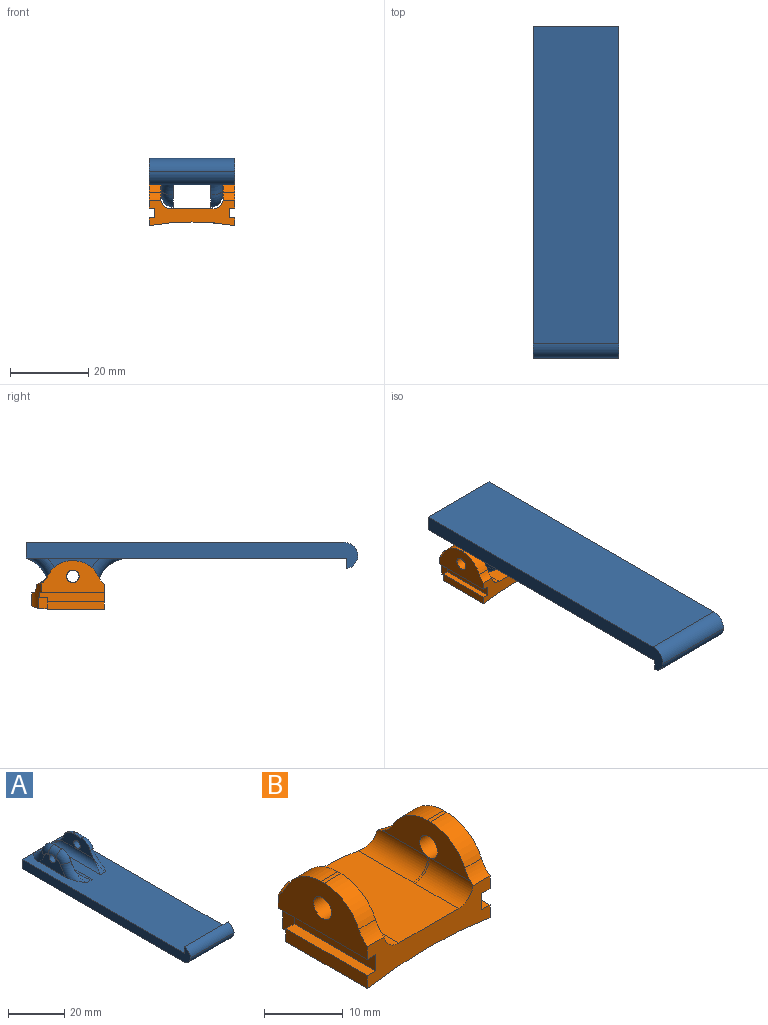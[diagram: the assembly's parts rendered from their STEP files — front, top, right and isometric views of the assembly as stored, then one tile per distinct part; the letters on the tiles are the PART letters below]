
ASSEMBLY  parts=2 mates=1
PART A: 36 faces, bbox 22x85x14.6 mm
  f0: plane 82x22mm, normal (0,0,1), area 1528.8mm2, adj f1,f2,f3,f5,f9,f17,f20,f22
  f1: plane 22x4mm, normal (0,1,0), area 88mm2, adj f0,f2,f3,f4,f21,f23
  f2: plane 84.99x6.8mm, normal (-1,0,0), area 342.9mm2, adj f0,f1,f4,f17,f18,f19
  f3: plane 84.99x6.8mm, normal (1,0,0), area 342.9mm2, adj f0,f1,f4,f17,f18,f19
  f4: plane 81.38x22mm, normal (0,0,-1), area 1790.3mm2, adj f1,f2,f3,f19
  f5: plane 13.57x5.6mm, normal (-1,0,0), area 46.2mm2, adj f0,f12,f31,f32,f33,f34,f35
  f6: plane 16.49x5.84mm, normal (1,0,0), area 65.3mm2, adj f7,f12,f13,f14,f20,f21,f24
  f7: plane 4x0.1mm, normal (0,0,1), area 0.4mm2, adj f6,f13,f14,f33
  f8: plane 16.49x5.84mm, normal (-1,0,0), area 65.3mm2, adj f10,f11,f15,f16,f22,f23,f25
  f9: plane 13.57x5.6mm, normal (1,0,0), area 46.2mm2, adj f0,f11,f26,f27,f28,f29,f30
  f10: plane 4x0.1mm, normal (0,0,1), area 0.4mm2, adj f8,f15,f16,f28
  f11: cylinder r=1.6mm len=3.2mm, axis (-1,0,0), area 30mm2, adj f8,f9,f28
  f12: cylinder r=1.6mm len=3.2mm, axis (-1,0,0), area 30mm2, adj f5,f6,f33
  f13: cylinder r=5mm len=4.65mm, axis (-1,0,0), area 0.6mm2, adj f6,f7,f20,f32
  f14: cylinder r=5mm len=4.71mm, axis (1,0,0), area 0.6mm2, adj f6,f7,f21,f34
  f15: cylinder r=5mm len=4.65mm, axis (-1,0,0), area 0.6mm2, adj f8,f10,f22,f27
  f16: cylinder r=5mm len=4.71mm, axis (1,0,0), area 0.6mm2, adj f8,f10,f23,f29
  f17: plane 22x2.8mm, normal (0,1,0), area 61.6mm2, adj f0,f2,f3,f18
  f18: cylinder r=3.62mm len=22mm, axis (-1,0,0), area 107.1mm2, adj f2,f3,f17,f19
  f19: cylinder r=3.62mm len=22mm, axis (1,0,0), area 120.9mm2, adj f2,f3,f4,f18
  f20: cylinder r=8.45mm len=7.86mm, axis (-1,0,0), area 8.1mm2, adj f0,f6,f13,f24,f31
  f21: cylinder r=8.45mm len=5.28mm, axis (-1,0,0), area 4.2mm2, adj f1,f6,f14,f24,f35
  f22: cylinder r=8.45mm len=7.86mm, axis (-1,0,0), area 8.1mm2, adj f0,f8,f15,f25,f26
  f23: cylinder r=8.45mm len=5.28mm, axis (-1,0,0), area 4.2mm2, adj f1,f8,f16,f25,f30
  f24: cylinder r=2.66mm len=26.49mm, axis (0,1,0), area 89.2mm2, adj f0,f6,f20,f21
  f25: cylinder r=2.66mm len=26.49mm, axis (0,-1,0), area 89.2mm2, adj f0,f8,f22,f23
  f26: torus R=11.35mm, axis (1,0,0), area 33.2mm2, adj f0,f9,f22,f27
  f27: torus R=2.1mm, axis (1,0,0), area 21.4mm2, adj f9,f15,f26,f28
  f28: cylinder r=2.9mm len=4mm, axis (0,-1,0), area 16.9mm2, adj f9,f10,f11,f27,f29
  f29: torus R=2.1mm, axis (1,0,0), area 22.1mm2, adj f9,f16,f28,f30
  f30: torus R=11.35mm, axis (1,0,0), area 29.4mm2, adj f0,f9,f23,f29
  f31: torus R=11.35mm, axis (1,0,0), area 33.2mm2, adj f0,f5,f20,f32
  f32: torus R=2.1mm, axis (1,0,0), area 21.4mm2, adj f5,f13,f31,f33
  f33: cylinder r=2.9mm len=4mm, axis (0,1,0), area 16.9mm2, adj f5,f7,f12,f32,f34
  f34: torus R=2.1mm, axis (1,0,0), area 22.1mm2, adj f5,f14,f33,f35
  f35: torus R=11.35mm, axis (1,0,0), area 29.4mm2, adj f0,f5,f21,f34
PART B: 42 faces, bbox 26.8x18.9x12.9 mm
  f0: cylinder r=25.41mm len=10.5mm, axis (0,0,1), area 41.3mm2, adj f3,f5,f10,f13,f14,f27,f33,f34
  f1: plane 22x6.5mm, normal (0,-1,0), area 88.9mm2, adj f6,f7,f8,f9,f10,f11,f12,f13
  f2: cylinder r=25.41mm len=10.5mm, axis (0,0,1), area 41.3mm2, adj f3,f4,f7,f11,f15,f29,f31,f34
  f3: plane 3.32x1mm, normal (0,1,0), area 3.3mm2, adj f0,f2,f34,f35
  f4: plane 2.76x2.06mm, normal (-1,0,0), area 5.7mm2, adj f2,f30,f31,f34
  f5: plane 2.76x2.06mm, normal (1,0,0), area 5.7mm2, adj f0,f32,f33,f34
  f6: plane 14.61x1.5mm, normal (0,0,1), area 21.9mm2, adj f1,f9,f13,f32
  f7: plane 16.66x2.5mm, normal (-1,0,0), area 39.6mm2, adj f1,f2,f12,f15,f30,f31
  f8: plane 14.61x2mm, normal (-1,0,0), area 29.2mm2, adj f1,f12,f30,f34
  f9: plane 14.61x2mm, normal (1,0,0), area 29.2mm2, adj f1,f6,f32,f34
  f10: plane 16.44x8.44mm, normal (1,0,0), area 90.2mm2, adj f0,f1,f14,f17,f20,f21,f25,f26
  f11: plane 16.45x8.45mm, normal (-1,0,0), area 90.2mm2, adj f1,f2,f15,f19,f22,f23,f24,f28
  f12: plane 14.61x1.5mm, normal (0,0,1), area 21.9mm2, adj f1,f7,f8,f30
  f13: plane 16.66x2.5mm, normal (1,0,0), area 39.6mm2, adj f0,f1,f6,f14,f32,f33
  f14: plane 16.66x1.5mm, normal (0,0,-1), area 24.5mm2, adj f0,f1,f10,f13
  f15: plane 16.66x1.5mm, normal (0,0,-1), area 24.5mm2, adj f1,f2,f7,f11
  f16: plane 15.81x5.62mm, normal (-1,0,0), area 52.3mm2, adj f17,f20,f21,f25,f26,f27,f36,f38
  f17: plane 3x0.57mm, normal (0,0,1), area 1.7mm2, adj f10,f16,f20,f21
  f18: plane 15.81x5.62mm, normal (1,0,0), area 52.3mm2, adj f19,f22,f23,f24,f28,f29,f39,f41
  f19: plane 3x0.57mm, normal (0,0,1), area 1.7mm2, adj f11,f18,f22,f23
  f20: cylinder r=6.76mm len=6.19mm, axis (1,0,0), area 23.5mm2, adj f10,f16,f17,f26
  f21: cylinder r=6.76mm len=6.12mm, axis (1,0,0), area 22.4mm2, adj f10,f16,f17,f27
  f22: cylinder r=6.76mm len=6.19mm, axis (1,0,0), area 23.5mm2, adj f11,f18,f19,f28
  f23: cylinder r=6.76mm len=6.12mm, axis (1,0,0), area 22.4mm2, adj f11,f18,f19,f29
  f24: cylinder r=1.6mm len=3.2mm, axis (-1,0,0), area 30.2mm2, adj f11,f18,f40
  f25: cylinder r=1.6mm len=3.2mm, axis (-1,0,0), area 30.2mm2, adj f10,f16,f37
  f26: cylinder r=5mm len=3.03mm, axis (-1,0,0), area 7.5mm2, adj f1,f10,f16,f20,f36
  f27: bspline ~6.44x3.38mm, area 10.4mm2, adj f0,f10,f16,f21,f38
  f28: cylinder r=5mm len=3.03mm, axis (-1,0,0), area 7.5mm2, adj f1,f11,f18,f22,f39
  f29: bspline ~6.44x3.38mm, area 10.4mm2, adj f2,f11,f18,f23,f41
  f30: plane 3x1.52mm, normal (0,1,0), area 2.9mm2, adj f4,f7,f8,f12,f31,f34
  f31: plane 2.06x0.02mm, normal (0,0,-1), area 0mm2, adj f2,f4,f7,f30
  f32: plane 3x1.52mm, normal (0,1,0), area 2.9mm2, adj f5,f6,f9,f13,f33,f34
  f33: plane 2.06x0.02mm, normal (0,0,-1), area 0mm2, adj f0,f5,f13,f32
  f34: cylinder r=65.51mm len=22mm, axis (0,1,0), area 380.5mm2, adj f0,f1,f2,f3,f4,f5,f8,f9
  f35: plane 18.5x10.69mm, normal (0,0,1), area 195.8mm2, adj f0,f1,f2,f3,f36,f37,f38,f39
  f36: cylinder r=2.66mm len=7.87mm, axis (0,-1,0), area 32.7mm2, adj f1,f16,f26,f35,f37
  f37: bspline ~2.7x2.7mm, area 1.1mm2, adj f25,f35,f36,f38
  f38: cylinder r=2.66mm len=9.8mm, axis (0,-1,0), area 39.1mm2, adj f0,f16,f27,f35,f37
  f39: cylinder r=2.66mm len=7.87mm, axis (0,1,0), area 32.7mm2, adj f1,f18,f28,f35,f40
  f40: bspline ~2.72x2.71mm, area 1.1mm2, adj f24,f35,f39,f41
  f41: cylinder r=2.66mm len=9.8mm, axis (0,1,0), area 39.1mm2, adj f2,f18,f29,f35,f40
PLACE A rot(axis=(0,1,0),180deg) t=(-12.58,-40.28,17.59)mm
PLACE B t=(-12.58,-17.91,6.25)mm
MATE revolute A.f11 <-> B.f24  axis (-1,0,0) through (-20.33,-28.41,8.89)mm
